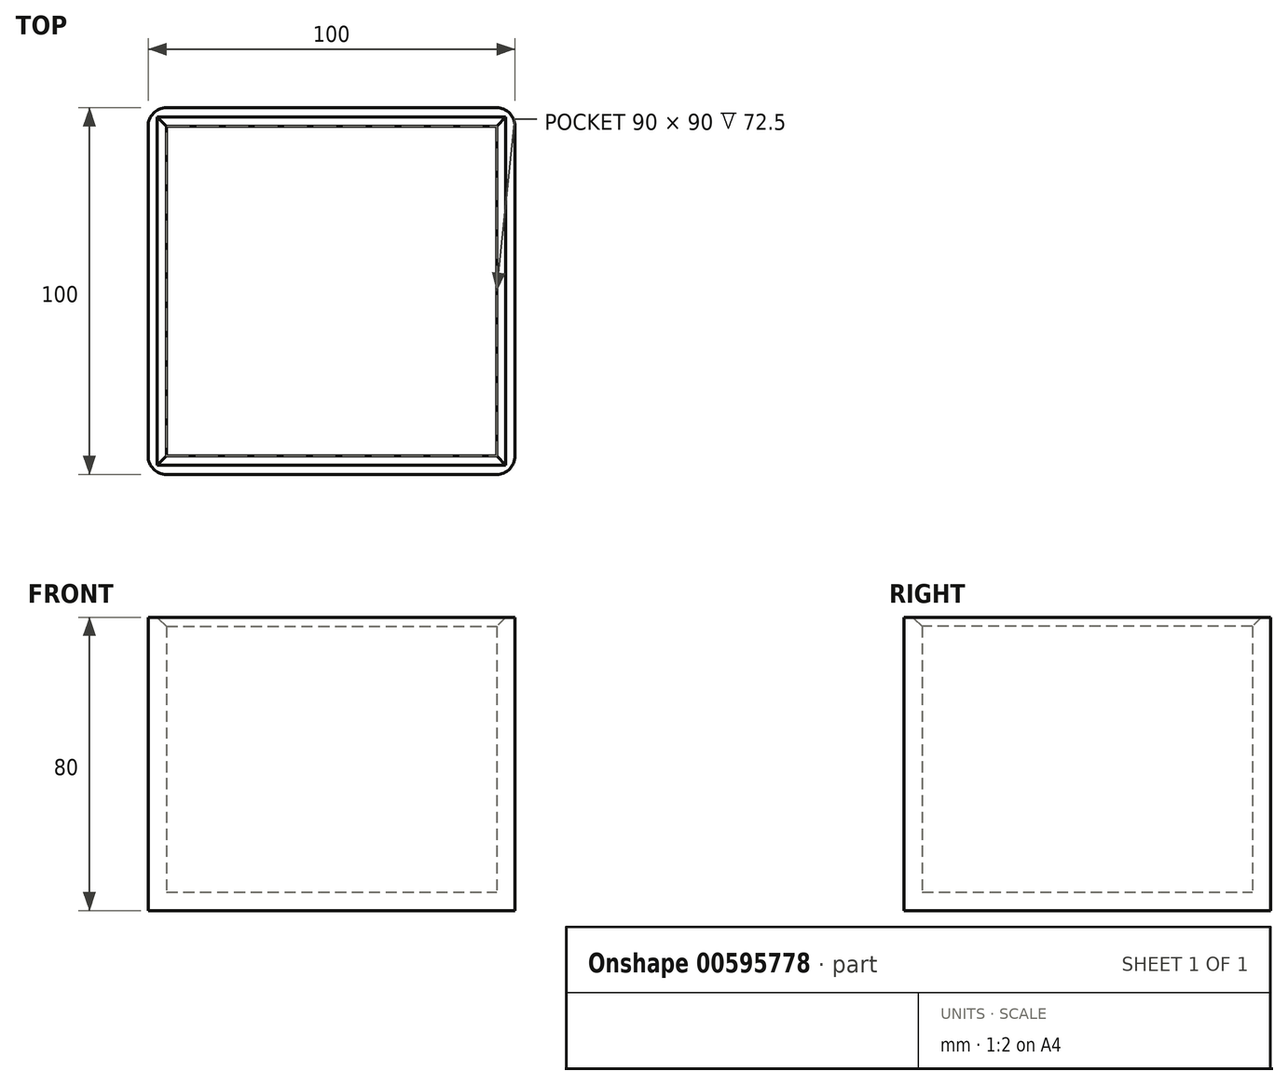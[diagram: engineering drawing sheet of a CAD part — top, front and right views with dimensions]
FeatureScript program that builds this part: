
annotation { "Feature Type Name" : "Feature", "Feature Type Description" : "" }
export const myFeature = defineFeature(function(context is Context, id is Id, definition is map)
    precondition{}
    {
        {
            var Q0;
            Q0=qCreatedBy(makeId("Front.planeOp"),FACE);
            var sketch = newSketch(context, id + "F0", { "sketchPlane" : qUnion([Q0])});
            skLineSegment(sketch, "E0.bottom", {"start": v(-48.44, 41.02) * mm, "end": v(51.56, 41.02) * mm});
            skLineSegment(sketch, "E0.top", {"start": v(-48.44, -38.98) * mm, "end": v(51.56, -38.98) * mm});
            skLineSegment(sketch, "E0.left", {"start": v(-48.44, 41.02) * mm, "end": v(-48.44, -38.98) * mm});
            skLineSegment(sketch, "E0.right", {"start": v(51.56, 41.02) * mm, "end": v(51.56, -38.98) * mm});
            skSolve(sketch);
        }
        {
            var Q0;
            Q0=makeQuery(id+"F0.imprint","IMPRINT",FACE,{"disambiguationData":[TD([[makeQuery(id+"F0.imprint","IMPRINT",EDGE,{"derivedFrom":sQuery(id+"F0.wireOp",EDGE,"E0.bottom")}),-1.0]])]});
            extrude(context, id + "F1", {"entities" : qUnion([Q0]), "depth" : 100 * mm, "offsetDistance" : 25 * mm});
        }
        {
            var Q0;
            Q0=makeQuery(id+"F1.opExtrude","SWEPT_FACE",FACE,{"disambiguationData":[OSD([sQuery(id+"F0.wireOp",EDGE,"E0.bottom")])]});
            shell(context, id + "F2", {"entities" : qUnion([Q0]), "thickness" : 5 * mm});
        }
        {
            var Q0;
            {var subQ0=sQuery(id+"F0.wireOp",EDGE,"E0.bottom");Q0=makeQuery(id+"F2.opShell","OFFSET_EDGE",EDGE,{"disambiguationData":[OSD([subQ0]),TDD([makeQuery(id+"F1.opExtrude","CAP_EDGE",EDGE,{"disambiguationData":[OSD([subQ0])],"isStart":true})])]});}
            var Q1;
            Q1=makeQuery(id+"F2.opShell","OFFSET_EDGE",EDGE,{"disambiguationData":[OSD([sQuery(id+"F0.wireOp",EDGE,"E0.bottom"),sQuery(id+"F0.wireOp",EDGE,"E0.left")])]});
            var Q2;
            {var subQ0=sQuery(id+"F0.wireOp",EDGE,"E0.bottom");Q2=makeQuery(id+"F2.opShell","OFFSET_EDGE",EDGE,{"disambiguationData":[OSD([subQ0]),TDD([makeQuery(id+"F1.opExtrude","CAP_EDGE",EDGE,{"disambiguationData":[OSD([subQ0])],"isStart":false})])]});}
            var Q3;
            Q3=makeQuery(id+"F2.opShell","OFFSET_EDGE",EDGE,{"disambiguationData":[OSD([sQuery(id+"F0.wireOp",EDGE,"E0.bottom"),sQuery(id+"F0.wireOp",EDGE,"E0.right")])]});
            chamfer(context, id + "F3", {"entities" : qUnion([Q0, Q1, Q2, Q3]), "width" : 2.5 * mm, "tangentPropagation" : true});
        }
        {
            var Q0;
            Q0=makeQuery(id+"F1.opExtrude","CAP_EDGE",EDGE,{"disambiguationData":[OSD([sQuery(id+"F0.wireOp",EDGE,"E0.left")])],"isStart":false});
            var Q1;
            Q1=makeQuery(id+"F1.opExtrude","CAP_EDGE",EDGE,{"disambiguationData":[OSD([sQuery(id+"F0.wireOp",EDGE,"E0.right")])],"isStart":false});
            var Q2;
            Q2=makeQuery(id+"F1.opExtrude","CAP_EDGE",EDGE,{"disambiguationData":[OSD([sQuery(id+"F0.wireOp",EDGE,"E0.right")])],"isStart":true});
            var Q3;
            Q3=makeQuery(id+"F1.opExtrude","CAP_EDGE",EDGE,{"disambiguationData":[OSD([sQuery(id+"F0.wireOp",EDGE,"E0.left")])],"isStart":true});
            fillet(context, id + "F4", {"entities" : qUnion([Q0, Q1, Q2, Q3]), "radius" : 5 * mm, "tangentPropagation" : true, "allowEdgeOverflow" : false});
        }
    });
